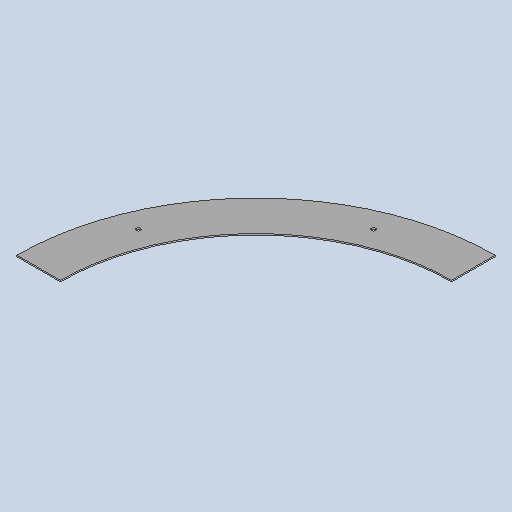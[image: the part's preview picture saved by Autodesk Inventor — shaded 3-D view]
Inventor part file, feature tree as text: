
AUTODESK INVENTOR PART (.ipt)
format: ipt  version: 2025 (Build 290162010, 162A)  size: 292,864 bytes
history: native  units: mm
features: other x3, sketch x2, sheet_metal_op x1, pattern_circular x1
ambient origin geometry x8: Origin, YZ Plane, XZ Plane, XY Plane, X Axis, Y Axis, Z Axis, Center Point
bodies: Solid1 (feature_tree)
feature tree (7):
  sheet_metal_op  "Face1"
  pattern_circular  "Circular Pattern1"  Count=110  [1 undecoded]
  sketch  "Sketch1"  dims[d1=900.0mm]
  other  "Plate1"
  sketch  "Sketch2"  dims[d2=3.0mm d4=10.0mm d5=22.5deg d6=3.0mm d7=0.0mm d8=20.0mm d9=45.0deg]
  other  "Cut1"
  other  "Definition1"
note: 1 required parameter value undecoded (feature->parameter linkage not recoverable at this tier; creation-order binding heuristic only, values carry confidence <= 0.55)
